# Revit family: Zumtobel LANOS
name_source: partatom
category: Lighting Fixtures
revit_build: Autodesk Revit 2018 (Build: 20170223_1515(x64)
units: mm (PartAtom-declared; Revit-internal decimal feet)

## family parameters
Cut with Voids When Loaded = No
Host = Face
Light Source = Yes
OmniClass Number = 23.80.70.11
OmniClass Title = Luminaries for Internal Lighting
Part Type = Normal
Room Calculation Point = No
Round Connector Dimension = Use Diameter
Shared = No

## types (3) — shared parameters
Assembly Code = D5020200
Color Filter = 16777215
Description = Decorative wall and ceiling mount LED luminaire
Dimming Lamp Color Temperature Shift = <None>
Emit Shape Visible in Rendering = No
Height = 69 mm
Lamp = LED
Manufacturer = Zumtobel Lighting
Tilt Angle = 90.00°
URL = http://www.zumtobel.com
Voltage = 230 V
zero-valued in all types: Default Elevation

## per-type parameters (varying)
| type | Apparent Load | Emit from Circle Diameter | Length | Model | Photometric Web File | Top Diameter | Width |
| LANOS M 3500-940 OP HL LDE WH | 25 VA | 376 mm | 396 mm | 42188187 | ZS_Lanos_400mm_HL_Full_3500lm.IES | 288 mm | 396 mm |
| LANOS L 4000-940 OP HL LDE WH | 31 VA | 476 mm | 496 mm | 42188223 | ZS_Lanos_500mm_HL_Full_4000lm.IES | 288 mm | 496 mm |
| LANOS S 1900-940 OP DI LDE WH | 15 VA | 300 mm | 320 mm | 42188119 | 42188119_(STD_LEO).IES | 248 mm | 320 mm |

## geometry (parser evidence)
native form markers: Sweep x3
no freeform markers — native parametric forms only
